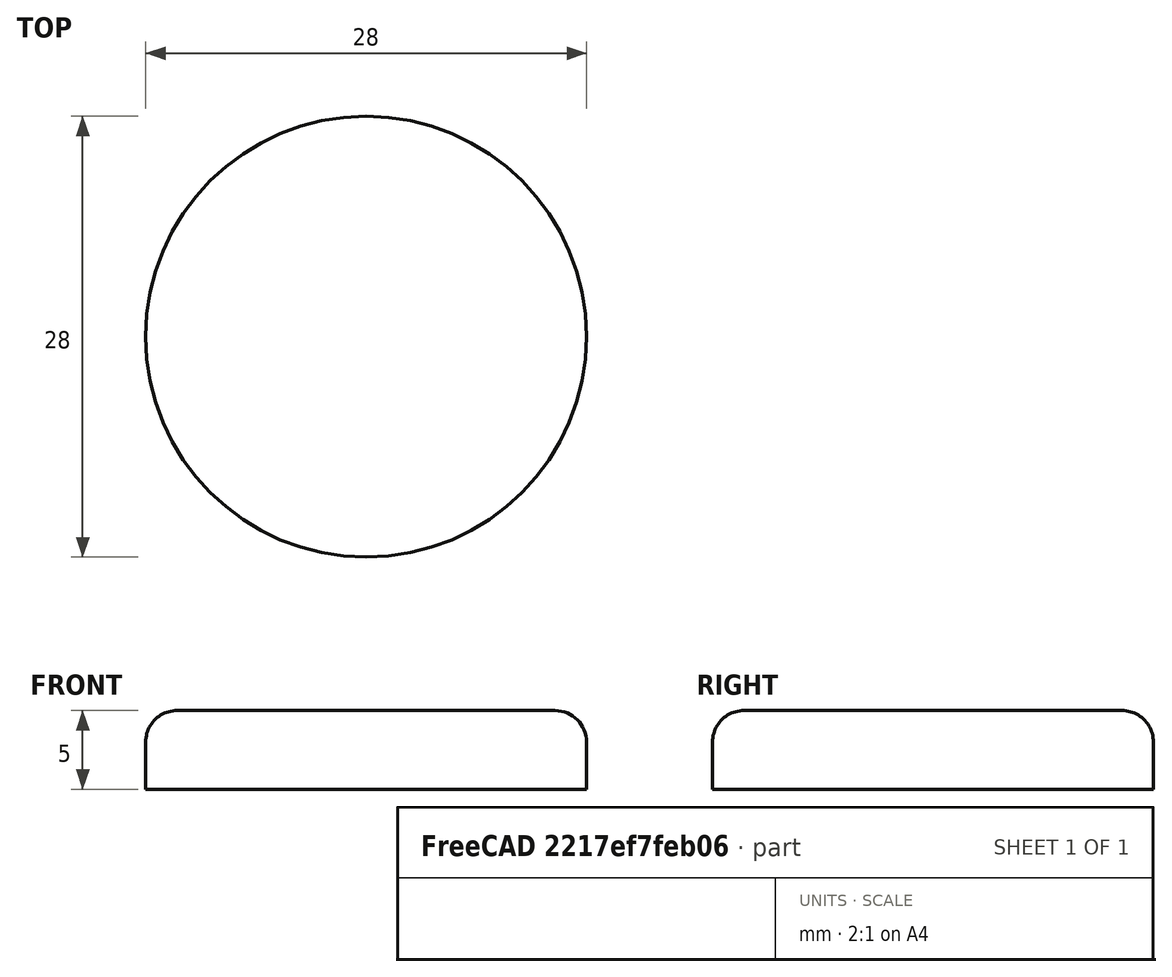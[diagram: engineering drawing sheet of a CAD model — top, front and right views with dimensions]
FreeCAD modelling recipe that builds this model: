
FCSTD DOCUMENT  (FreeCAD 1.0R39109 (Git))
Label: top
License: All rights reserved
LicenseURL: https://en.wikipedia.org/wiki/All_rights_reserved
objects: Sketcher::SketchObject×1, PartDesign::Pad×1, PartDesign::Fillet×1, PartDesign::Body×1
note: 9 computed .brp shape members not serialized (recipe doc carries the construction recipe); baked Part::Feature solids carry a one-line shape summary decoded from their .brp

FEATURE [Sketcher::SketchObject] Sketch
  ArcFitTolerance = 1e-06
  AttachmentSupport = -> [XY_Plane]
  FullyConstrained = false
  MakeInternals = false
  MapMode = 5
  sketch-geometry (1):
    g0: Circle CenterX=-0.073484 CenterY=0 CenterZ=0 NormalX=0 NormalY=0 NormalZ=1 AngleXU=0 Radius=14
  constraints (2):
    c: Diameter(g0) = 28
    c: PointOnObject(g0,g-1)
FEATURE [PartDesign::Pad] Pad
  Direction = (0,0,1)
  Length = 5
  Length2 = 10
  Profile = -> Sketch
  ReferenceAxis = -> Sketch [N_Axis]
  Refine = true
  Suppressed = false
  Type = 0
FEATURE [PartDesign::Fillet] Fillet
  Base = -> Pad [Edge3]
  BaseFeature = -> Pad
  Radius = 2
  Refine = true
  SupportTransform = false
  Suppressed = false
  UseAllEdges = false
FEATURE [PartDesign::Body] Body
  AllowCompound = false
  Group = -> [Sketch,Pad,Fillet]
  Origin = -> Origin
  Tip = -> Fillet
